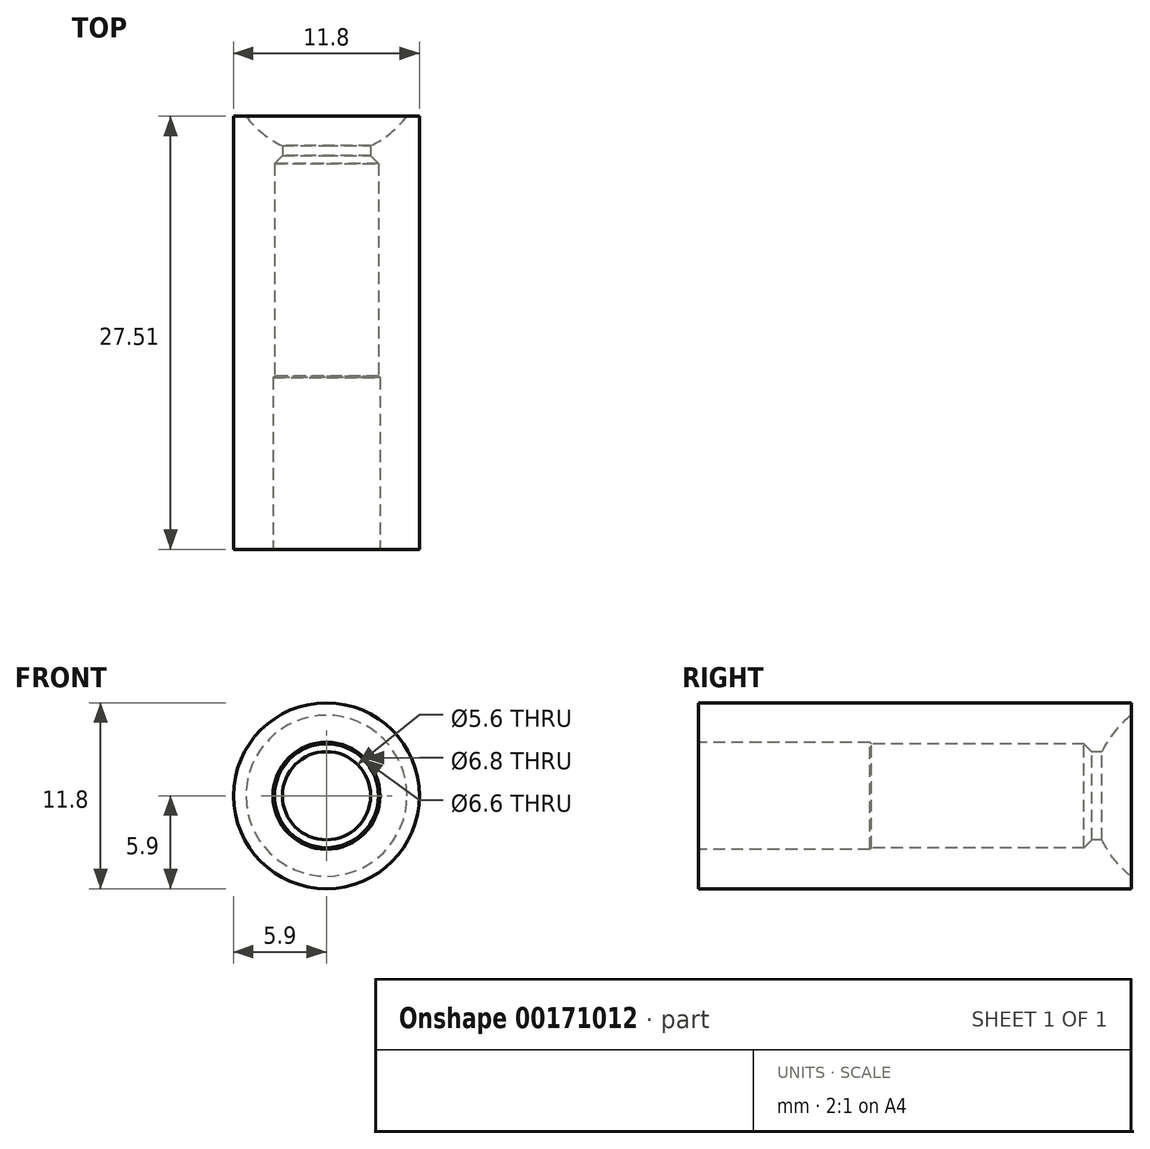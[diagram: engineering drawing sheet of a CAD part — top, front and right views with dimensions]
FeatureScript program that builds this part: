
annotation { "Feature Type Name" : "Feature", "Feature Type Description" : "" }
export const myFeature = defineFeature(function(context is Context, id is Id, definition is map)
    precondition{}
    {
        {
            var Q0;
            Q0=qCreatedBy(makeId("Right.planeOp"),FACE);
            var sketch = newSketch(context, id + "F0", { "sketchPlane" : qUnion([Q0])});
            skCircle(sketch, "E0", {"center": v(13.4, 0) * mm, "radius": 6.48 * mm});
            skLineSegment(sketch, "E1.bottom", {"start": v(-6.42, -3.3) * mm, "end": v(6.43, -3.3) * mm});
            skLineSegment(sketch, "E1.top", {"start": v(-6.43, 3.3) * mm, "end": v(6.42, 3.3) * mm});
            skLineSegment(sketch, "E1.left", {"start": v(-6.43, -3.3) * mm, "end": v(-6.43, 3.3) * mm});
            skLineSegment(sketch, "E1.right", {"start": v(6.43, -3.3) * mm, "end": v(6.42, 3.3) * mm});
            skPoint(sketch, "E1.middle", {"position": v(0, 0) * mm});
            skLineSegment(sketch, "E2.bottom", {"start": v(-18.07, -3.4) * mm, "end": v(-7.07, -3.4) * mm});
            skLineSegment(sketch, "E2.top", {"start": v(-18.07, 3.4) * mm, "end": v(-7.08, 3.4) * mm});
            skLineSegment(sketch, "E2.left", {"start": v(-18.07, -3.4) * mm, "end": v(-18.07, 3.4) * mm});
            skLineSegment(sketch, "E2.right", {"start": v(-7.08, -3.4) * mm, "end": v(-7.08, 3.4) * mm});
            skPoint(sketch, "E2.middle", {"position": v(-12.58, 0) * mm});
            skLineSegment(sketch, "E3", {"start": v(0, 0) * mm, "end": v(2.4, 0) * mm, "construction": true});
            skLineSegment(sketch, "E4", {"start": v(6.42, 1.5) * mm, "end": v(7.1, 1.5) * mm});
            skLineSegment(sketch, "E5", {"start": v(-18.07, 3.4) * mm, "end": v(-18.07, 5.9) * mm});
            skLineSegment(sketch, "E6", {"start": v(-18.07, 5.9) * mm, "end": v(10.73, 5.9) * mm});
            skLineSegment(sketch, "E7", {"start": v(-6.43, 3.3) * mm, "end": v(-7.08, 3.3) * mm});
            skLineSegment(sketch, "E8", {"start": v(9.42, 5.9) * mm, "end": v(9.42, 5.11) * mm});
            skPoint(sketch, "E9.endSnap0", {"position": v(6.43, 0) * mm});
            skPoint(sketch, "E9.endSnap1", {"position": v(6.76, 1.5) * mm});
            skLineSegment(sketch, "E10", {"start": v(6.93, 3.3) * mm, "end": v(6.93, 0) * mm});
            skLineSegment(sketch, "E11", {"start": v(6.93, 3.3) * mm, "end": v(6.42, 3.3) * mm});
            skLineSegment(sketch, "E12", {"start": v(6.42, 3.3) * mm, "end": v(6.92, 2.8) * mm});
            skLineSegment(sketch, "E13", {"start": v(6.92, 2.8) * mm, "end": v(7.56, 2.8) * mm});
            skSolve(sketch);
        }
        {
            var Q0;
            {var subQ0=sQuery(id+"F0.wireOp",EDGE,"E11");Q0=makeQuery(id+"F0.imprint","IMPRINT",FACE,{"disambiguationData":[TD([[makeQuery(id+"F0.imprint","IMPRINT",EDGE,{"derivedFrom":subQ0}),1.0]])]});}
            var Q1;
            Q1=makeQuery(id+"F0.imprint","IMPRINT",FACE,{"disambiguationData":[TD([[makeQuery(id+"F0.imprint","IMPRINT",EDGE,{"derivedFrom":sQuery(id+"F0.wireOp",EDGE,"E1.top")}),1.0]])]});
            var Q2;
            Q2=sQuery(id+"F0.wireOp",EDGE,"E3");
            revolve(context, id + "F1", {"entities" : qUnion([Q0, Q1]), "axis" : qUnion([Q2]), "revolveType" : RevolveType.FULL});
        }
        {
            var Q0;
            Q0=makeQuery(id+"F1.opRevolve","SWEPT_EDGE",EDGE,{"disambiguationData":[OSD([sQuery(id+"F0.wireOp",EDGE,"E2.top"),sQuery(id+"F0.wireOp",EDGE,"E2.right")])]});
            chamfer(context, id + "F2", {"entities" : qUnion([Q0]), "width" : .1 * mm, "tangentPropagation" : true});
        }
    });
